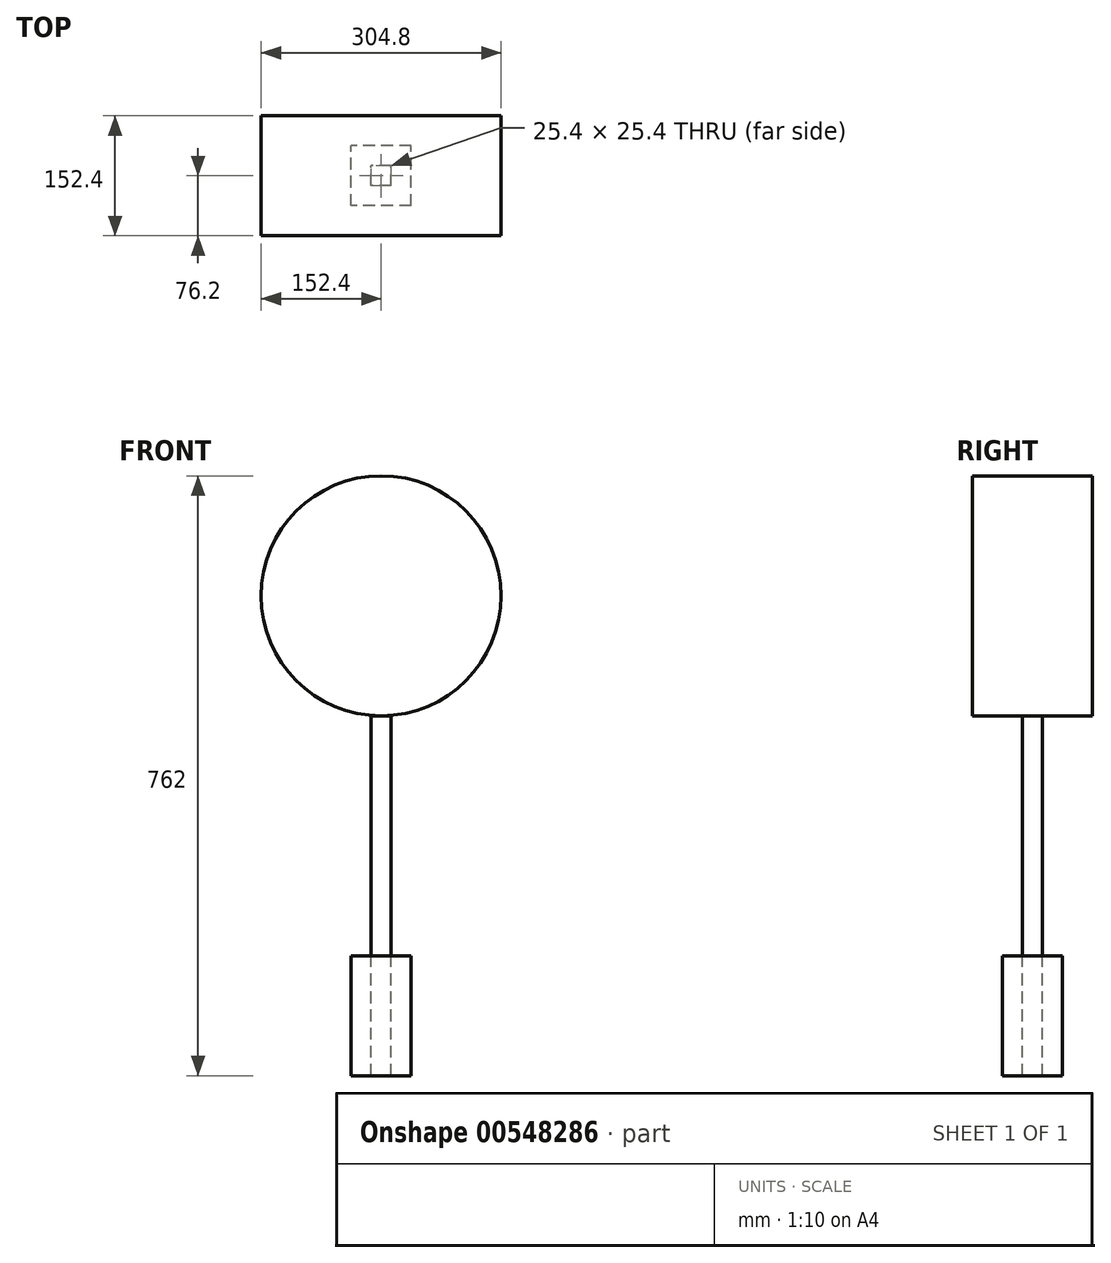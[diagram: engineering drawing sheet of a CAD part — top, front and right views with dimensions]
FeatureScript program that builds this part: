
annotation { "Feature Type Name" : "Feature", "Feature Type Description" : "" }
export const myFeature = defineFeature(function(context is Context, id is Id, definition is map)
    precondition{}
    {
        {
            var Q0;
            Q0=qCreatedBy(makeId("Front.planeOp"),FACE);
            var sketch = newSketch(context, id + "F0", { "sketchPlane" : qUnion([Q0])});
            skCircle(sketch, "E0", {"center": v(0, 0) * mm, "radius": 152.4 * mm});
            skSolve(sketch);
        }
        {
            var Q0;
            Q0=makeQuery(id+"F0.imprint","IMPRINT",FACE,{"disambiguationData":[TD([[makeQuery(id+"F0.imprint","IMPRINT",EDGE,{"derivedFrom":sQuery(id+"F0.wireOp",EDGE,"E0")}),1.0]])]});
            extrude(context, id + "F1", {"entities" : qUnion([Q0]), "endBound" : BoundingType.SYMMETRIC, "depth" : 152.4 * mm, "offsetDistance" : 25.4 * mm});
        }
        {
            var Q0;
            Q0=qCreatedBy(makeId("Top.planeOp"),FACE);
            cPlane(context, id + "F2", {"entities" : qUnion([Q0]), "cplaneType" : CPlaneType.OFFSET, "offset" : 152.4 * mm, "oppositeDirection" : true, "width" : 152.4 * mm, "height" : 152.4 * mm});
        }
        {
            var Q0;
            Q0=qCreatedBy(id+"F2.planeOp",FACE);
            var sketch = newSketch(context, id + "F3", { "sketchPlane" : qUnion([Q0])});
            skLineSegment(sketch, "E1.bottom", {"start": v(12.7, -12.7) * mm, "end": v(-12.7, -12.7) * mm});
            skLineSegment(sketch, "E1.top", {"start": v(12.7, 12.7) * mm, "end": v(-12.7, 12.7) * mm});
            skLineSegment(sketch, "E1.left", {"start": v(12.7, -12.7) * mm, "end": v(12.7, 12.7) * mm});
            skLineSegment(sketch, "E1.right", {"start": v(-12.7, -12.7) * mm, "end": v(-12.7, 12.7) * mm});
            skPoint(sketch, "E1.middle", {"position": v(0, 0) * mm});
            skSolve(sketch);
        }
        {
            var Q0;
            Q0=makeQuery(id+"F3.imprint","IMPRINT",FACE,{"disambiguationData":[TD([[makeQuery(id+"F3.imprint","IMPRINT",EDGE,{"derivedFrom":sQuery(id+"F3.wireOp",EDGE,"E1.bottom")}),-1.0]])]});
            extrude(context, id + "F4", {"entities" : qUnion([Q0]), "operationType" : NewBodyOperationType.ADD, "oppositeDirection" : true, "depth" : 304.8 * mm, "offsetDistance" : 25.4 * mm});
        }
        {
            var Q0;
            Q0=makeQuery(id+"F4.opExtrude","CAP_FACE",FACE,{"disambiguationData":[OSD([sQuery(id+"F3.wireOp",EDGE,"E1.bottom"),sQuery(id+"F3.wireOp",EDGE,"E1.top"),sQuery(id+"F3.wireOp",EDGE,"E1.left"),sQuery(id+"F3.wireOp",EDGE,"E1.right")])],"isStart":false});
            var sketch = newSketch(context, id + "F5", { "sketchPlane" : qUnion([Q0])});
            skLineSegment(sketch, "E2.bottom", {"start": v(38.1, 38.1) * mm, "end": v(-38.1, 38.1) * mm});
            skLineSegment(sketch, "E2.top", {"start": v(38.1, -38.1) * mm, "end": v(-38.1, -38.1) * mm});
            skLineSegment(sketch, "E2.left", {"start": v(38.1, 38.1) * mm, "end": v(38.1, -38.1) * mm});
            skLineSegment(sketch, "E2.right", {"start": v(-38.1, 38.1) * mm, "end": v(-38.1, -38.1) * mm});
            skPoint(sketch, "E2.middle", {"position": v(0, 0) * mm});
            skSolve(sketch);
        }
        {
            var Q0;
            Q0=makeQuery(id+"F5.imprint","IMPRINT",FACE,{"disambiguationData":[TD([[makeQuery(id+"F5.imprint","IMPRINT",EDGE,{"derivedFrom":sQuery(id+"F5.wireOp",EDGE,"E2.bottom")}),1.0]])]});
            extrude(context, id + "F6", {"entities" : qUnion([Q0]), "depth" : 152.4 * mm, "offsetDistance" : 25.4 * mm});
        }
    });
